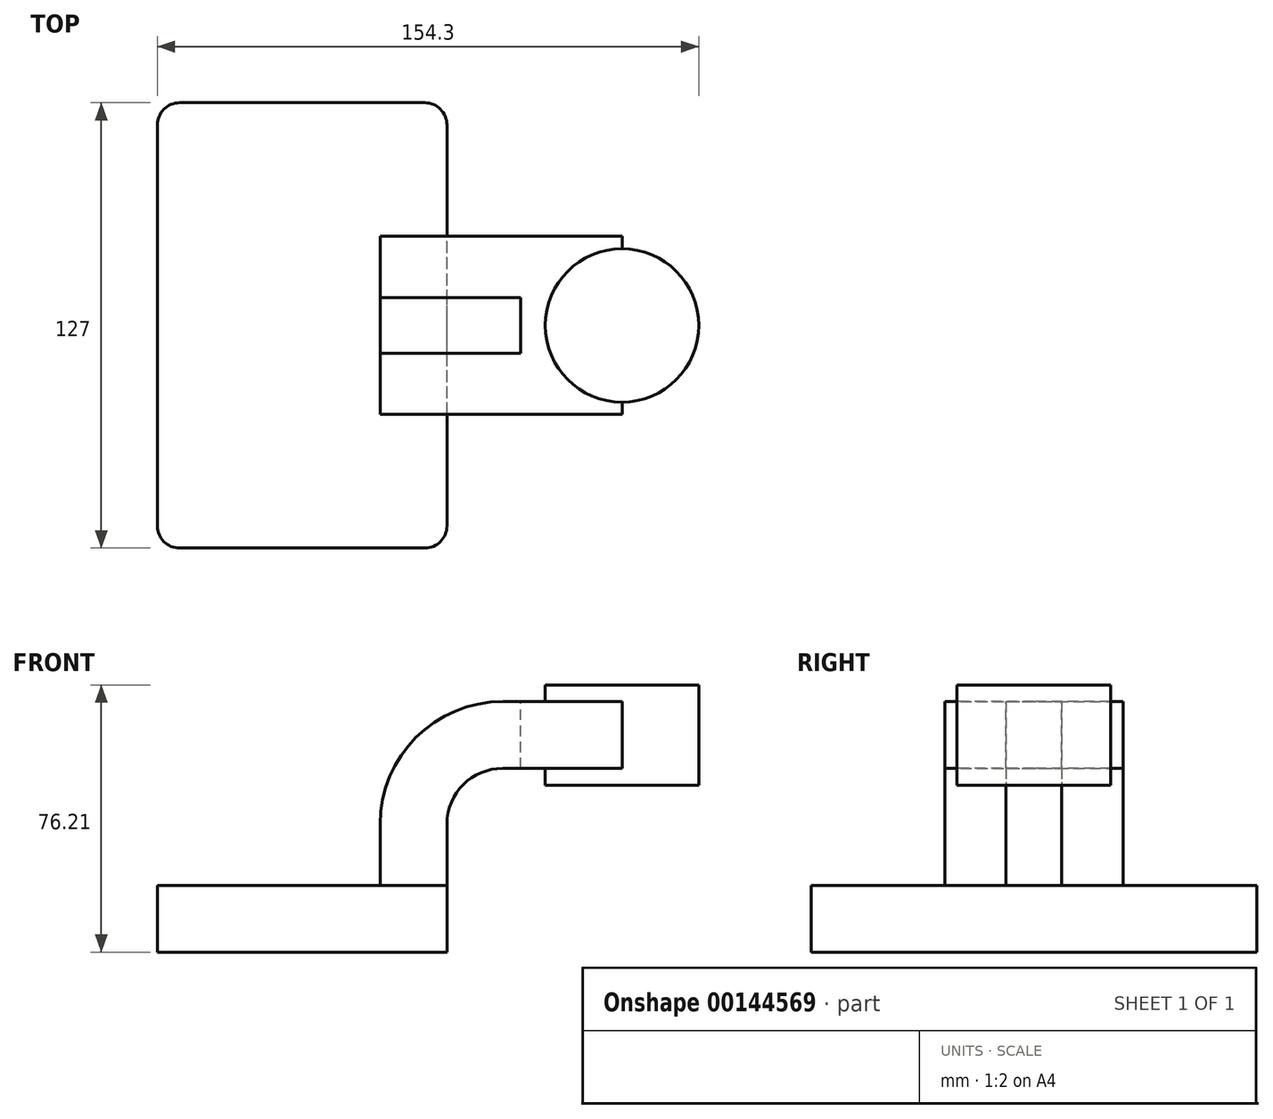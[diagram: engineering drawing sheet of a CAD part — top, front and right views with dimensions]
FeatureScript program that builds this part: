
annotation { "Feature Type Name" : "Feature", "Feature Type Description" : "" }
export const myFeature = defineFeature(function(context is Context, id is Id, definition is map)
    precondition{}
    {
        {
            var Q0;
            Q0=qCreatedBy(makeId("Front.planeOp"),FACE);
            var sketch = newSketch(context, id + "F0", { "sketchPlane" : qUnion([Q0])});
            skLineSegment(sketch, "E0.bottom", {"start": v(41.28, 9.53) * mm, "end": v(-41.28, 9.52) * mm});
            skLineSegment(sketch, "E0.top", {"start": v(41.28, -9.52) * mm, "end": v(-41.28, -9.53) * mm});
            skLineSegment(sketch, "E0.left", {"start": v(41.27, 9.53) * mm, "end": v(41.28, -9.52) * mm});
            skLineSegment(sketch, "E0.right", {"start": v(-41.28, 9.52) * mm, "end": v(-41.28, -9.53) * mm});
            skPoint(sketch, "E0.middle", {"position": v(0, 0) * mm});
            skLineSegment(sketch, "E1.bottom", {"start": v(113.03, 38.1) * mm, "end": v(62.23, 38.1) * mm});
            skLineSegment(sketch, "E1.top", {"start": v(113.03, 66.68) * mm, "end": v(62.23, 66.68) * mm});
            skLineSegment(sketch, "E1.left", {"start": v(113.03, 38.1) * mm, "end": v(113.03, 66.68) * mm});
            skLineSegment(sketch, "E1.right", {"start": v(62.23, 38.1) * mm, "end": v(62.23, 66.68) * mm});
            skPoint(sketch, "E1.middle", {"position": v(87.63, 52.39) * mm});
            skLineSegment(sketch, "E2", {"start": v(41.28, 9.53) * mm, "end": v(41.28, 27) * mm});
            skArc(sketch, "E3", {"start": v(41.27, 27) * mm, "mid": v(45.92, 38.23) * mm, "end": v(57.15, 42.88) * mm});
            skLineSegment(sketch, "E4", {"start": v(57.15, 42.88) * mm, "end": v(62.23, 42.88) * mm});
            skLineSegment(sketch, "E5.0", {"start": v(57.15, 61.93) * mm, "end": v(91.16, 61.93) * mm});
            skArc(sketch, "E5.1", {"start": v(22.23, 27) * mm, "mid": v(32.45, 51.7) * mm, "end": v(57.15, 61.93) * mm});
            skLineSegment(sketch, "E5.2", {"start": v(22.23, 9.53) * mm, "end": v(22.23, 27) * mm});
            skFitSpline(sketch, "E6", {"points": [v(-41.28, 9.52) * mm, v(57.15, 61.93) * mm], "startDerivative": vector(-0.55, 53.32) * mm, "endDerivative": vector(147.8, -2.1) * mm});
            skLineSegment(sketch, "E7", {"start": v(62.23, 42.88) * mm, "end": v(91.16, 42.88) * mm});
            skLineSegment(sketch, "E8", {"start": v(91.16, 42.88) * mm, "end": v(91.16, 61.93) * mm});
            skLineSegment(sketch, "E9", {"start": v(91.16, 61.93) * mm, "end": v(91.16, 66.68) * mm});
            skLineSegment(sketch, "E10", {"start": v(91.16, 42.88) * mm, "end": v(91.16, 38.1) * mm});
            skSolve(sketch);
        }
        {
            var Q0;
            Q0=makeQuery(id+"F0.imprint","IMPRINT",FACE,{"disambiguationData":[TD([[makeQuery(id+"F0.imprint","IMPRINT",EDGE,{"derivedFrom":sQuery(id+"F0.wireOp",EDGE,"E0.top")}),-1.0]])]});
            extrude(context, id + "F1", {"entities" : qUnion([Q0]), "endBound" : BoundingType.SYMMETRIC, "depth" : 127 * mm});
        }
        {
            var Q0;
            {var subQ1=sQuery(id+"F0.wireOp",EDGE,"E2");Q0=makeQuery(id+"F0.imprint","IMPRINT",FACE,{"disambiguationData":[TD([[makeQuery(id+"F0.imprint","IMPRINT",EDGE,{"derivedFrom":subQ1}),1.0]])]});}
            var Q1;
            {var subQ0=sQuery(id+"F0.wireOp",EDGE,"E7");Q1=makeQuery(id+"F0.imprint","IMPRINT",FACE,{"disambiguationData":[TD([[makeQuery(id+"F0.imprint","IMPRINT",EDGE,{"derivedFrom":subQ0}),1.0]])]});}
            var Q2;
            Q2=sQuery(id+"F0.wireOp",EDGE,"E3");
            var Q3;
            Q3=sQuery(id+"F0.wireOp",EDGE,"E5.1");
            var Q4;
            Q4=sQuery(id+"F0.wireOp",EDGE,"E5.0");
            var Q5;
            Q5=sQuery(id+"F0.wireOp",EDGE,"E4");
            var Q6;
            Q6=sQuery(id+"F0.wireOp",EDGE,"E7");
            var Q7;
            Q7=sQuery(id+"F0.wireOp",EDGE,"E8");
            var Q8;
            Q8=sQuery(id+"F0.wireOp",EDGE,"E5.2");
            var Q9;
            Q9=sQuery(id+"F0.wireOp",EDGE,"E2");
            var Q10;
            Q10=sQuery(id+"F0.wireOp",EDGE,"E0.bottom");
            extrude(context, id + "F2", {"entities" : qUnion([Q0, Q1]), "surfaceEntities" : qUnion([Q2, Q3, Q4, Q5, Q6, Q7, Q8, Q9, Q10]), "endBound" : BoundingType.SYMMETRIC, "depth" : 50.8 * mm});
        }
        {
            var Q0;
            Q0=makeQuery(id+"F0.imprint","IMPRINT",FACE,{"disambiguationData":[TD([[makeQuery(id+"F0.imprint","IMPRINT",EDGE,{"derivedFrom":sQuery(id+"F0.wireOp",EDGE,"E5.1")}),1.0]])]});
            extrude(context, id + "F3", {"entities" : qUnion([Q0]), "endBound" : BoundingType.SYMMETRIC, "depth" : 15.88 * mm});
        }
        {
            var Q0;
            {var subQ0=sQuery(id+"F0.wireOp",EDGE,"E1.left");Q0=makeQuery(id+"F0.imprint","IMPRINT",FACE,{"disambiguationData":[TD([[makeQuery(id+"F0.imprint","IMPRINT",EDGE,{"derivedFrom":subQ0}),1.0]])]});}
            var Q1;
            Q1=sQuery(id+"F0.wireOp",EDGE,"E8");
            revolve(context, id + "F4", {"operationType" : NewBodyOperationType.ADD, "entities" : qUnion([Q0]), "axis" : qUnion([Q1]), "revolveType" : RevolveType.FULL});
        }
        {
            var Q0;
            Q0=makeQuery(id+"F1.opExtrude","CAP_EDGE",EDGE,{"disambiguationData":[OSD([sQuery(id+"F0.wireOp",EDGE,"E0.left")])],"isStart":false});
            fillet(context, id + "F5", {"entities" : qUnion([Q0]), "radius" : 6.35 * mm, "tangentPropagation" : true, "allowEdgeOverflow" : false});
        }
        {
            var Q0;
            Q0=makeQuery(id+"F1.opExtrude","CAP_EDGE",EDGE,{"disambiguationData":[OSD([sQuery(id+"F0.wireOp",EDGE,"E0.right")])],"isStart":false});
            fillet(context, id + "F6", {"entities" : qUnion([Q0]), "radius" : 6.35 * mm, "tangentPropagation" : true, "allowEdgeOverflow" : false});
        }
        {
            var Q0;
            Q0=makeQuery(id+"F1.opExtrude","CAP_EDGE",EDGE,{"disambiguationData":[OSD([sQuery(id+"F0.wireOp",EDGE,"E0.right")])],"isStart":true});
            var Q1;
            Q1=makeQuery(id+"F1.opExtrude","CAP_EDGE",EDGE,{"disambiguationData":[OSD([sQuery(id+"F0.wireOp",EDGE,"E0.left")])],"isStart":true});
            fillet(context, id + "F7", {"entities" : qUnion([Q0, Q1]), "radius" : 6.35 * mm, "tangentPropagation" : true, "allowEdgeOverflow" : false});
        }
    });
